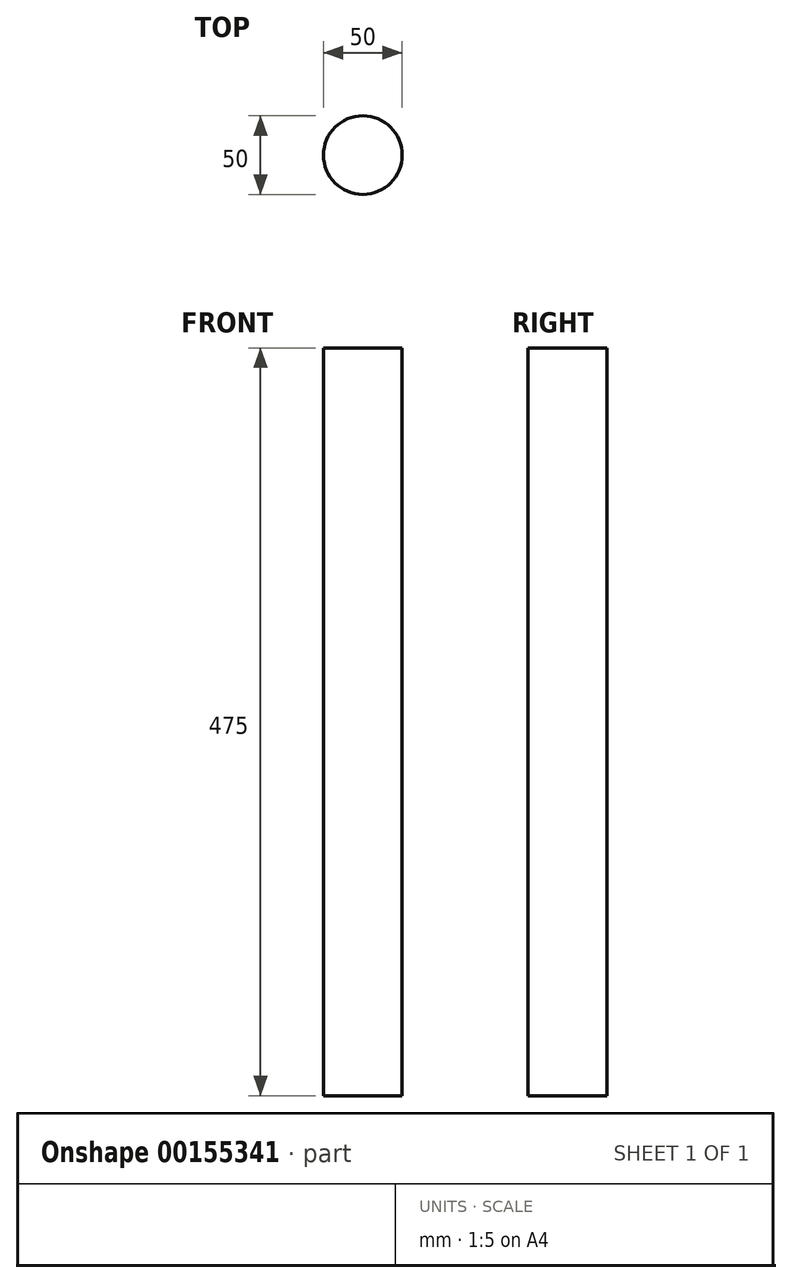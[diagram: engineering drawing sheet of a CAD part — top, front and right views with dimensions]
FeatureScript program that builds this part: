
annotation { "Feature Type Name" : "Feature", "Feature Type Description" : "" }
export const myFeature = defineFeature(function(context is Context, id is Id, definition is map)
    precondition{}
    {
        {
            var Q0;
            Q0=qCreatedBy(makeId("Top.planeOp"),FACE);
            var sketch = newSketch(context, id + "F0", { "sketchPlane" : qUnion([Q0])});
            skCircle(sketch, "E0", {"center": v(0, 0) * mm, "radius": 25 * mm});
            skSolve(sketch);
        }
        {
            var Q0;
            Q0=makeQuery(id+"F0.imprint","IMPRINT",FACE,{"disambiguationData":[TD([[makeQuery(id+"F0.imprint","IMPRINT",EDGE,{"derivedFrom":sQuery(id+"F0.wireOp",EDGE,"E0")}),1.0]])]});
            extrude(context, id + "F1", {"entities" : qUnion([Q0]), "depth" : 475 * mm});
        }
    });
